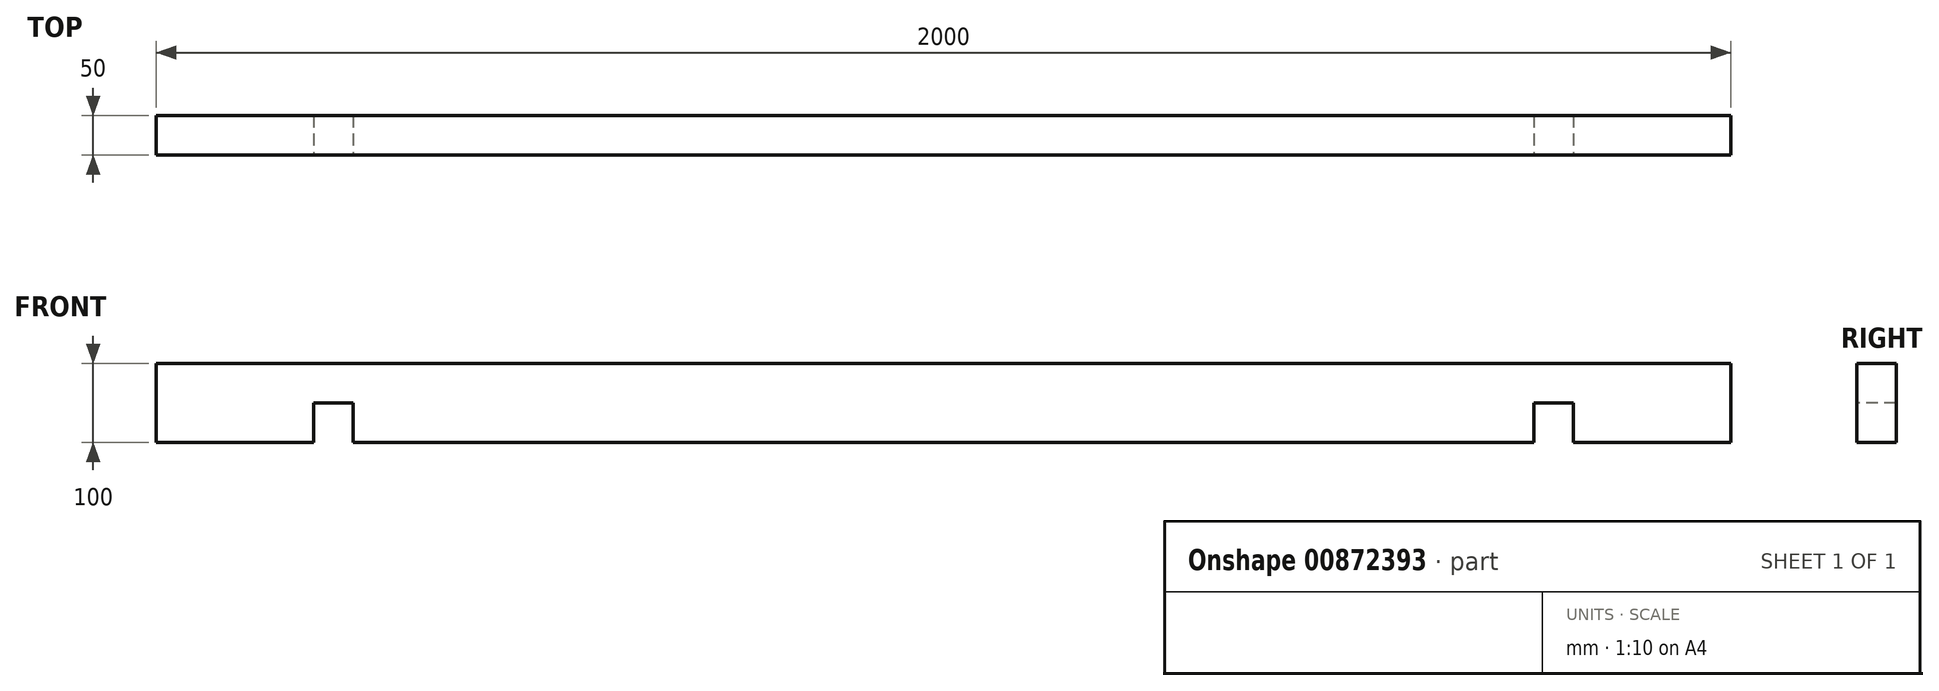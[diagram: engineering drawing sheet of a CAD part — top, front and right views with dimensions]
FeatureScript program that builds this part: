
annotation { "Feature Type Name" : "Feature", "Feature Type Description" : "" }
export const myFeature = defineFeature(function(context is Context, id is Id, definition is map)
    precondition{}
    {
        {
            var Q0;
            Q0=qCreatedBy(makeId("Right.planeOp"),FACE);
            var sketch = newSketch(context, id + "F0", { "sketchPlane" : qUnion([Q0])});
            skLineSegment(sketch, "E0.bottom", {"start": v(-25, 50) * mm, "end": v(25, 50) * mm});
            skLineSegment(sketch, "E0.top", {"start": v(-25, -50) * mm, "end": v(25, -50) * mm});
            skLineSegment(sketch, "E0.left", {"start": v(-25, 50) * mm, "end": v(-25, -50) * mm});
            skLineSegment(sketch, "E0.right", {"start": v(25, 50) * mm, "end": v(25, -50) * mm});
            skSolve(sketch);
        }
        {
            var Q0;
            Q0=qSketchRegion(id+"F0",true);
            extrude(context, id + "F1", {"entities" : qUnion([Q0]), "depth" : 2000 * mm, "offsetDistance" : 25 * mm});
        }
        {
            var Q0;
            Q0=makeQuery(id+"F1.opExtrude","SWEPT_BODY",BODY,{"disambiguationData":[OSD([sQuery(id+"F0.wireOp",EDGE,"E0.bottom"),sQuery(id+"F0.wireOp",EDGE,"E0.top"),sQuery(id+"F0.wireOp",EDGE,"E0.left"),sQuery(id+"F0.wireOp",EDGE,"E0.right")])]});
            transform(context, id + "F2", {"entities" : qUnion([Q0]), "transformType" : TransformType.TRANSLATION_3D, "dx" : 0 * mm, "dy" : 2000 * mm, "dz" : 0 * mm, "makeCopy" : true});
        }
        {
            var Q0;
            Q0=makeQuery(id+"F1.opExtrude","SWEPT_BODY",BODY,{"disambiguationData":[OSD([sQuery(id+"F0.wireOp",EDGE,"E0.bottom"),sQuery(id+"F0.wireOp",EDGE,"E0.top"),sQuery(id+"F0.wireOp",EDGE,"E0.left"),sQuery(id+"F0.wireOp",EDGE,"E0.right")])]});
            var Q1;
            Q1=makeQuery(id+"F1.opExtrude","CAP_EDGE",EDGE,{"disambiguationData":[OSD([sQuery(id+"F0.wireOp",EDGE,"E0.left")])],"isStart":true});
            transform(context, id + "F3", {"entities" : qUnion([Q0]), "transformType" : TransformType.ROTATION, "transformAxis" : qUnion([Q1]), "angle" : 90 * degree, "oppositeDirection" : true, "makeCopy" : true});
        }
        {
            var Q0;
            Q0=makeQuery(id+"F3.opPattern","COPY",BODY,{"derivedFrom":makeQuery(id+"F1.opExtrude","SWEPT_BODY",BODY,{"disambiguationData":[OSD([sQuery(id+"F0.wireOp",EDGE,"E0.bottom"),sQuery(id+"F0.wireOp",EDGE,"E0.top"),sQuery(id+"F0.wireOp",EDGE,"E0.left"),sQuery(id+"F0.wireOp",EDGE,"E0.right")])]}),"instanceName":"1"});
            deleteBodies(context, id + "F4", {"entities" : qUnion([Q0])});
        }
        {
            var Q0;
            Q0=makeQuery(id+"F1.opExtrude","SWEPT_BODY",BODY,{"disambiguationData":[OSD([sQuery(id+"F0.wireOp",EDGE,"E0.bottom"),sQuery(id+"F0.wireOp",EDGE,"E0.top"),sQuery(id+"F0.wireOp",EDGE,"E0.left"),sQuery(id+"F0.wireOp",EDGE,"E0.right")])]});
            transform(context, id + "F5", {"entities" : qUnion([Q0]), "transformType" : TransformType.TRANSLATION_3D, "dx" : 0 * mm, "dy" : 0 * mm, "dz" : 0 * mm, "makeCopy" : true});
        }
        {
            var Q0;
            Q0=makeQuery(id+"F5.opPattern","COPY",BODY,{"derivedFrom":makeQuery(id+"F1.opExtrude","SWEPT_BODY",BODY,{"disambiguationData":[OSD([sQuery(id+"F0.wireOp",EDGE,"E0.bottom"),sQuery(id+"F0.wireOp",EDGE,"E0.top"),sQuery(id+"F0.wireOp",EDGE,"E0.left"),sQuery(id+"F0.wireOp",EDGE,"E0.right")])]}),"instanceName":"1"});
            deleteBodies(context, id + "F6", {"entities" : qUnion([Q0])});
        }
        {
            var Q0;
            Q0=makeQuery(id+"F2.opPattern","COPY",BODY,{"derivedFrom":makeQuery(id+"F1.opExtrude","SWEPT_BODY",BODY,{"disambiguationData":[OSD([sQuery(id+"F0.wireOp",EDGE,"E0.bottom"),sQuery(id+"F0.wireOp",EDGE,"E0.top"),sQuery(id+"F0.wireOp",EDGE,"E0.left"),sQuery(id+"F0.wireOp",EDGE,"E0.right")])]}),"instanceName":"1"});
            deleteBodies(context, id + "F7", {"entities" : qUnion([Q0])});
        }
        {
            var Q0;
            Q0=makeQuery(id+"F1.opExtrude","SWEPT_FACE",FACE,{"disambiguationData":[OSD([sQuery(id+"F0.wireOp",EDGE,"E0.left")])]});
            var sketch = newSketch(context, id + "F8", { "sketchPlane" : qUnion([Q0])});
            skLineSegment(sketch, "E1.bottom", {"start": v(200, -50) * mm, "end": v(250, -50) * mm});
            skLineSegment(sketch, "E1.top", {"start": v(200, 0) * mm, "end": v(250, 0) * mm});
            skLineSegment(sketch, "E1.left", {"start": v(200, -50) * mm, "end": v(200, 0) * mm});
            skLineSegment(sketch, "E1.right", {"start": v(250, -50) * mm, "end": v(250, 0) * mm});
            skLineSegment(sketch, "E2.bottom", {"start": v(1750, -50) * mm, "end": v(1800, -50) * mm});
            skLineSegment(sketch, "E2.top", {"start": v(1750, 0) * mm, "end": v(1800, 0) * mm});
            skLineSegment(sketch, "E2.left", {"start": v(1750, -50) * mm, "end": v(1750, 0) * mm});
            skLineSegment(sketch, "E2.right", {"start": v(1800, -50) * mm, "end": v(1800, 0) * mm});
            skSolve(sketch);
        }
        {
            var Q0;
            Q0 = qSketchRegion(id + "F8", true);
            extrude(context, id + "F9", {"entities" : qUnion([Q0]), "operationType" : NewBodyOperationType.REMOVE, "endBound" : BoundingType.THROUGH_ALL, "oppositeDirection" : true, "depth" : 25 * mm, "offsetDistance" : 25 * mm});
        }
    });
